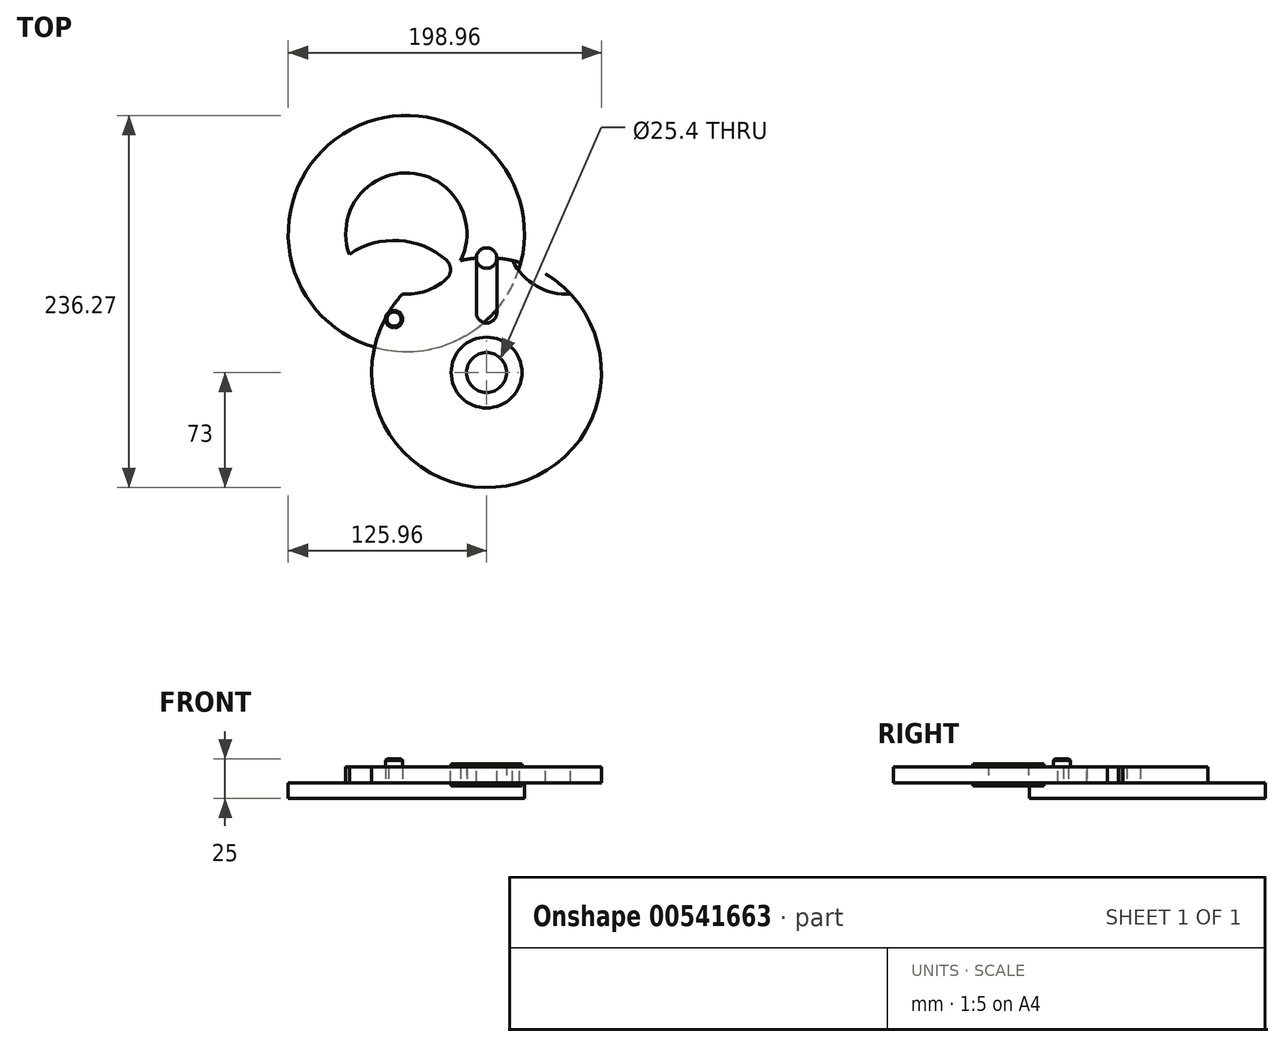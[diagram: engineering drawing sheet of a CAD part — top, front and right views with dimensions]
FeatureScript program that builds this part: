
annotation { "Feature Type Name" : "Feature", "Feature Type Description" : "" }
export const myFeature = defineFeature(function(context is Context, id is Id, definition is map)
    precondition{}
    {
        {
            var Q0;
            Q0=qCreatedBy(makeId("Top.planeOp"),FACE);
            var sketch = newSketch(context, id + "F0", { "sketchPlane" : qUnion([Q0])});
            skCircle(sketch, "E0", {"center": v(0, 0) * mm, "radius": 73 * mm});
            skSolve(sketch);
        }
        {
            var Q0;
            Q0 = qSketchRegion(id + "F0", true);
            extrude(context, id + "F1", {"entities" : qUnion([Q0]), "endBound" : BoundingType.SYMMETRIC, "depth" : 10 * mm, "offsetDistance" : 25 * mm, "hasSecondDirection" : true, "secondDirectionOppositeDirection" : true, "secondDirectionDepth" : 5 * mm});
        }
        {
            var Q0;
            Q0=qCreatedBy(makeId("Top.planeOp"),FACE);
            var sketch = newSketch(context, id + "F2", { "sketchPlane" : qUnion([Q0])});
            skCircle(sketch, "E1", {"center": v(0, 0) * mm, "radius": 38.5 * mm, "construction": true});
            skLineSegment(sketch, "E2", {"start": v(-6.5, 37.95) * mm, "end": v(-6.5, 72.71) * mm});
            skLineSegment(sketch, "E3", {"start": v(6.5, 72.71) * mm, "end": v(6.5, 37.95) * mm});
            skArc(sketch, "E4", {"start": v(6.5, 72.71) * mm, "mid": v(0, 79.21) * mm, "end": v(-6.5, 72.71) * mm});
            skArc(sketch, "E5", {"start": v(-6.5, 37.95) * mm, "mid": v(0, 31.45) * mm, "end": v(6.5, 37.95) * mm});
            skSolve(sketch);
        }
        {
            var Q0;
            Q0 = qSketchRegion(id + "F2", true);
            extrude(context, id + "F3", {"entities" : qUnion([Q0]), "operationType" : NewBodyOperationType.REMOVE, "endBound" : BoundingType.THROUGH_ALL, "oppositeDirection" : true, "depth" : 25 * mm, "offsetDistance" : 25 * mm, "hasSecondDirection" : true, "secondDirectionBound" : SecondDirectionBoundingType.THROUGH_ALL, "secondDirectionOppositeDirection" : false, "secondDirectionDepth" : 25 * mm});
        }
        {
            var Q0;
            Q0=qCreatedBy(makeId("Front.planeOp"),FACE);
            var sketch = newSketch(context, id + "F4", { "sketchPlane" : qUnion([Q0])});
            skLineSegment(sketch, "E6", {"start": v(0, 0) * mm, "end": v(0, 40.63) * mm, "construction": true});
            skSolve(sketch);
        }
        {
            var Q0;
            Q0=qCreatedBy(makeId("Top.planeOp"),FACE);
            var sketch = newSketch(context, id + "F5", { "sketchPlane" : qUnion([Q0])});
            skArc(sketch, "E7", {"start": v(16.5, 71.11) * mm, "mid": v(31.71, 54.93) * mm, "end": v(53.33, 49.84) * mm});
            skArc(sketch, "E8", {"start": v(53.33, 49.84) * mm, "mid": v(36.5, 63.22) * mm, "end": v(16.5, 71.11) * mm});
            skSolve(sketch);
        }
        {
            var Q0;
            Q0 = qSketchRegion(id + "F5", true);
            extrude(context, id + "F6", {"entities" : qUnion([Q0]), "operationType" : NewBodyOperationType.REMOVE, "endBound" : BoundingType.SYMMETRIC, "oppositeDirection" : true, "depth" : 10 * mm, "offsetDistance" : 25 * mm});
        }
        {
            var Q0;
            Q0=qCreatedBy(makeId("Top.planeOp"),FACE);
            var sketch = newSketch(context, id + "F7", { "sketchPlane" : qUnion([Q0])});
            skCircle(sketch, "E9", {"center": v(0, 0) * mm, "radius": 22.5 * mm});
            skCircle(sketch, "E10", {"center": v(0, 0) * mm, "radius": 12.7 * mm});
            skLineSegment(sketch, "E11", {"start": v(-3.25, 12.28) * mm, "end": v(-3.25, 15.53) * mm});
            skLineSegment(sketch, "E12", {"start": v(-3.25, 15.53) * mm, "end": v(3.25, 15.53) * mm});
            skLineSegment(sketch, "E13", {"start": v(3.25, 15.53) * mm, "end": v(3.25, 12.28) * mm});
            skSolve(sketch);
        }
        {
            var Q0;
            Q0 = qSketchRegion(id + "F7", true);
            extrude(context, id + "F8", {"entities" : qUnion([Q0]), "operationType" : NewBodyOperationType.ADD, "endBound" : BoundingType.SYMMETRIC, "depth" : 14 * mm, "offsetDistance" : 25 * mm});
        }
        {
            var Q0;
            Q0=makeQuery(id+"F8.boolean.opBoolean","SPLIT",FACE,{"disambiguationData":[TD([makeQuery(id+"F8.opExtrude","SWEPT_FACE",FACE,{"disambiguationData":[OSD([sQuery(id+"F7.wireOp",EDGE,"E10")])]})])],"derivedFrom":makeQuery(id+"F1.opExtrude","CAP_FACE",FACE,{"disambiguationData":[OSD([sQuery(id+"F0.wireOp",EDGE,"E0")])],"isStart":false})});
            extrude(context, id + "F9", {"entities" : qUnion([Q0]), "operationType" : NewBodyOperationType.REMOVE, "endBound" : BoundingType.THROUGH_ALL, "oppositeDirection" : true, "depth" : 25 * mm, "offsetDistance" : 25 * mm});
        }
        {
            var Q0;
            Q0=qCreatedBy(makeId("Top.planeOp"),FACE);
            var sketch = newSketch(context, id + "F10", { "sketchPlane" : qUnion([Q0])});
            skCircle(sketch, "E14", {"center": v(-50.96, 88.27) * mm, "radius": 38.5 * mm});
            skSolve(sketch);
        }
        {
            var Q0;
            Q0=makeQuery(id+"F10.imprint","IMPRINT",FACE,{"disambiguationData":[TD([[makeQuery(id+"F10.imprint","IMPRINT",EDGE,{"derivedFrom":sQuery(id+"F10.wireOp",EDGE,"E14")}),1.0]])]});
            extrude(context, id + "F11", {"entities" : qUnion([Q0]), "endBound" : BoundingType.SYMMETRIC, "depth" : 10 * mm, "offsetDistance" : 25 * mm});
        }
        {
            var Q0;
            Q0=makeQuery(id+"F11.opExtrude","CAP_FACE",FACE,{"disambiguationData":[OSD([sQuery(id+"F10.wireOp",EDGE,"E14")])],"isStart":true});
            var sketch = newSketch(context, id + "F12", { "sketchPlane" : qUnion([Q0])});
            skCircle(sketch, "E15", {"center": v(-50.96, -88.27) * mm, "radius": 75 * mm});
            skSolve(sketch);
        }
        {
            var Q0;
            Q0 = qSketchRegion(id + "F12", true);
            extrude(context, id + "F13", {"entities" : qUnion([Q0]), "operationType" : NewBodyOperationType.ADD, "depth" : 10 * mm, "offsetDistance" : 25 * mm});
        }
        {
            var Q0;
            Q0=makeQuery(id+"F13.opExtrude","CAP_FACE",FACE,{"disambiguationData":[OSD([sQuery(id+"F12.wireOp",EDGE,"E15")])],"isStart":true});
            var sketch = newSketch(context, id + "F14", { "sketchPlane" : qUnion([Q0])});
            skLineSegment(sketch, "E16", {"start": v(0, 0) * mm, "end": v(-73.55, 42.47) * mm, "construction": true});
            skCircle(sketch, "E17", {"center": v(-58.75, 33.92) * mm, "radius": 5.5 * mm});
            skSolve(sketch);
        }
        {
            var Q0;
            Q0 = qSketchRegion(id + "F14", true);
            extrude(context, id + "F15", {"entities" : qUnion([Q0]), "operationType" : NewBodyOperationType.ADD, "depth" : 15 * mm, "offsetDistance" : 25 * mm});
        }
        {
            var Q0;
            Q0=makeQuery(id+"F13.opExtrude","CAP_FACE",FACE,{"disambiguationData":[OSD([sQuery(id+"F12.wireOp",EDGE,"E15")])],"isStart":true});
            var sketch = newSketch(context, id + "F16", { "sketchPlane" : qUnion([Q0])});
            skArc(sketch, "E18", {"start": v(-19.95, 65.46) * mm, "mid": v(-51.66, 83.42) * mm, "end": v(-87.14, 75.09) * mm});
            skArc(sketch, "E19.0", {"start": v(-87.14, 75.09) * mm, "mid": v(-56.43, 50.16) * mm, "end": v(-19.95, 65.46) * mm});
            skSolve(sketch);
        }
        {
            var Q0;
            Q0 = qSketchRegion(id + "F16", true);
            extrude(context, id + "F17", {"entities" : qUnion([Q0]), "operationType" : NewBodyOperationType.REMOVE, "endBound" : BoundingType.THROUGH_ALL, "depth" : 25 * mm, "offsetDistance" : 25 * mm});
        }
        {
            var Q0;
            {var subQ0=sQuery(id+"F16.wireOp",EDGE,"E19.0");var subQ1=sQuery(id+"F16.wireOp",EDGE,"E18");var subQ2=sQuery(id+"F10.wireOp",EDGE,"E14");Q0=makeQuery(id+"F17.boolean.opBoolean","COPY",EDGE,{"derivedFrom":makeQuery(id+"F17.opExtrude","SWEPT_EDGE",EDGE,{"disambiguationData":[OSD([subQ2,subQ1,subQ0]),TDD([makeQuery(id+"F16.imprint","INTERSECT",VERTEX,{"disambiguationData":[OD(1.0)],"derivedFrom":[makeQuery(id+"F11.opExtrude","CAP_EDGE",EDGE,{"disambiguationData":[OSD([subQ2])],"isStart":true}),subQ1,subQ0]})])]})});}
            var Q1;
            {var subQ0=sQuery(id+"F16.wireOp",EDGE,"E19.0");var subQ1=sQuery(id+"F16.wireOp",EDGE,"E18");var subQ2=sQuery(id+"F10.wireOp",EDGE,"E14");Q1=makeQuery(id+"F17.boolean.opBoolean","COPY",EDGE,{"derivedFrom":makeQuery(id+"F17.opExtrude","SWEPT_EDGE",EDGE,{"disambiguationData":[OSD([subQ2,subQ1,subQ0]),TDD([makeQuery(id+"F16.imprint","INTERSECT",VERTEX,{"disambiguationData":[OD(0.0)],"derivedFrom":[makeQuery(id+"F11.opExtrude","CAP_EDGE",EDGE,{"disambiguationData":[OSD([subQ2])],"isStart":true}),subQ1,subQ0]})])]})});}
            fillet(context, id + "F18", {"entities" : qUnion([Q0, Q1]), "radius" : 8 * mm, "tangentPropagation" : true, "allowEdgeOverflow" : false});
        }
        {
            var Q0;
            Q0=makeQuery(id+"F15.opExtrude","CAP_EDGE",EDGE,{"disambiguationData":[OSD([sQuery(id+"F14.wireOp",EDGE,"E17")])],"isStart":false});
            chamfer(context, id + "F19", {"entities" : qUnion([Q0]), "width" : 1 * mm, "tangentPropagation" : true});
        }
    });
